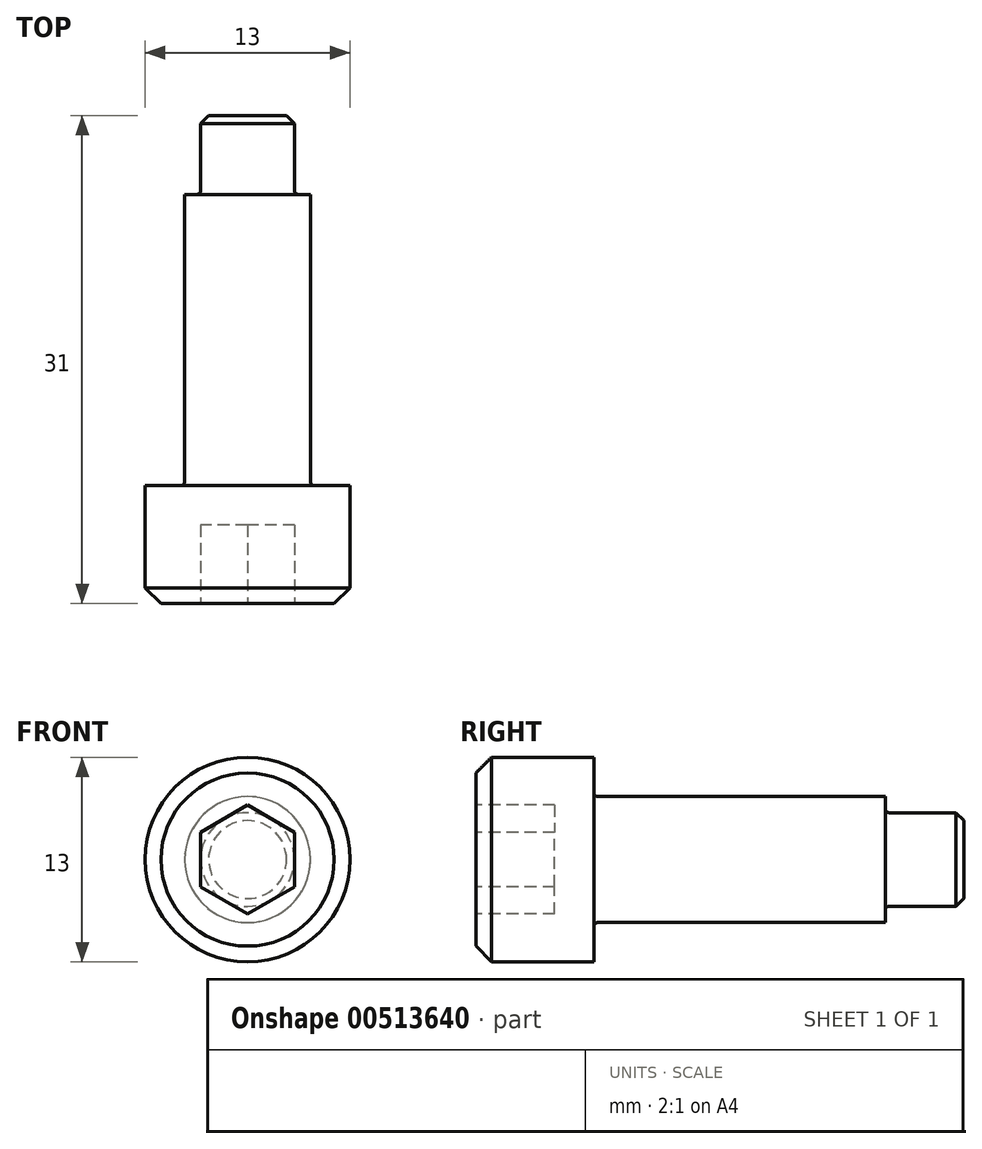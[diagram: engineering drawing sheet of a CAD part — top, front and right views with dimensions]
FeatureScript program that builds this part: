
annotation { "Feature Type Name" : "Feature", "Feature Type Description" : "" }
export const myFeature = defineFeature(function(context is Context, id is Id, definition is map)
    precondition{}
    {
        {
            var Q0;
            Q0=qCreatedBy(makeId("Top.planeOp"),FACE);
            var sketch = newSketch(context, id + "F0", { "sketchPlane" : qUnion([Q0])});
            skLineSegment(sketch, "E0", {"start": v(0, 0) * mm, "end": v(6.5, 0) * mm});
            skLineSegment(sketch, "E1", {"start": v(6.5, 0) * mm, "end": v(6.5, 7.5) * mm});
            skLineSegment(sketch, "E2", {"start": v(6.5, 7.5) * mm, "end": v(4, 7.5) * mm});
            skLineSegment(sketch, "E3", {"start": v(4, 7.5) * mm, "end": v(4, 26) * mm});
            skLineSegment(sketch, "E4", {"start": v(4, 26) * mm, "end": v(2.97, 26) * mm});
            skLineSegment(sketch, "E5", {"start": v(2.97, 26) * mm, "end": v(2.97, 31) * mm});
            skLineSegment(sketch, "E6", {"start": v(2.97, 31) * mm, "end": v(0, 31) * mm});
            skLineSegment(sketch, "E7", {"start": v(0, 31) * mm, "end": v(0, 0) * mm});
            skSolve(sketch);
        }
        {
            var Q0;
            Q0=makeQuery(id+"F0.imprint","IMPRINT",FACE,{"disambiguationData":[TD([[makeQuery(id+"F0.imprint","IMPRINT",EDGE,{"derivedFrom":sQuery(id+"F0.wireOp",EDGE,"E0")}),1.0]])]});
            var Q1;
            Q1=sQuery(id+"F0.wireOp",EDGE,"E7");
            revolve(context, id + "F1", {"entities" : qUnion([Q0]), "axis" : qUnion([Q1]), "revolveType" : RevolveType.FULL});
        }
        {
            var Q0;
            Q0=makeQuery(id+"F1.opRevolve","SWEPT_EDGE",EDGE,{"disambiguationData":[OSD([sQuery(id+"F0.wireOp",EDGE,"E2"),sQuery(id+"F0.wireOp",EDGE,"E3")])]});
            var Q1;
            Q1=makeQuery(id+"F1.opRevolve","SWEPT_EDGE",EDGE,{"disambiguationData":[OSD([sQuery(id+"F0.wireOp",EDGE,"E4"),sQuery(id+"F0.wireOp",EDGE,"E5")])]});
            fillet(context, id + "F2", {"entities" : qUnion([Q0, Q1]), "radius" : 0.25 * mm, "tangentPropagation" : true, "allowEdgeOverflow" : false});
        }
        {
            var Q0;
            Q0=makeQuery(id+"F1.opRevolve","SWEPT_EDGE",EDGE,{"disambiguationData":[OSD([sQuery(id+"F0.wireOp",EDGE,"E5"),sQuery(id+"F0.wireOp",EDGE,"E6")])]});
            chamfer(context, id + "F3", {"entities" : qUnion([Q0]), "width" : 0.5 * mm, "tangentPropagation" : true});
        }
        {
            var Q0;
            Q0=makeQuery(id+"F1.opRevolve","SWEPT_EDGE",EDGE,{"disambiguationData":[OSD([sQuery(id+"F0.wireOp",EDGE,"E0"),sQuery(id+"F0.wireOp",EDGE,"E1")])]});
            chamfer(context, id + "F4", {"entities" : qUnion([Q0]), "width" : 1 * mm, "tangentPropagation" : true});
        }
        {
            var Q0;
            Q0=makeQuery(id+"F1.opRevolve","SWEPT_FACE",FACE,{"disambiguationData":[OSD([sQuery(id+"F0.wireOp",EDGE,"E0")])]});
            var sketch = newSketch(context, id + "F5", { "sketchPlane" : qUnion([Q0])});
            skCircle(sketch, "E8.cCircle", {"center": v(0, 0) * mm, "radius": 3 * mm, "construction": true});
            skLineSegment(sketch, "E8.0", {"start": v(-3, -1.73) * mm, "end": v(-3, 1.73) * mm});
            skLineSegment(sketch, "E8.1", {"start": v(-3, 1.73) * mm, "end": v(0, 3.46) * mm});
            skLineSegment(sketch, "E8.2", {"start": v(0, 3.46) * mm, "end": v(3, 1.73) * mm});
            skLineSegment(sketch, "E8.3", {"start": v(3, 1.73) * mm, "end": v(3, -1.73) * mm});
            skLineSegment(sketch, "E8.4", {"start": v(3, -1.73) * mm, "end": v(0, -3.46) * mm});
            skLineSegment(sketch, "E8.5", {"start": v(0, -3.46) * mm, "end": v(-3, -1.73) * mm});
            skPoint(sketch, "E8.0.midPoint", {"position": v(-3, 0) * mm});
            skSolve(sketch);
        }
        {
            var Q0;
            Q0=makeQuery(id+"F5.imprint","IMPRINT",FACE,{"disambiguationData":[TD([[makeQuery(id+"F5.imprint","IMPRINT",EDGE,{"derivedFrom":sQuery(id+"F5.wireOp",EDGE,"E8.0")}),-1.0]])]});
            extrude(context, id + "F6", {"entities" : qUnion([Q0]), "operationType" : NewBodyOperationType.REMOVE, "oppositeDirection" : true, "depth" : 5 * mm});
        }
    });
